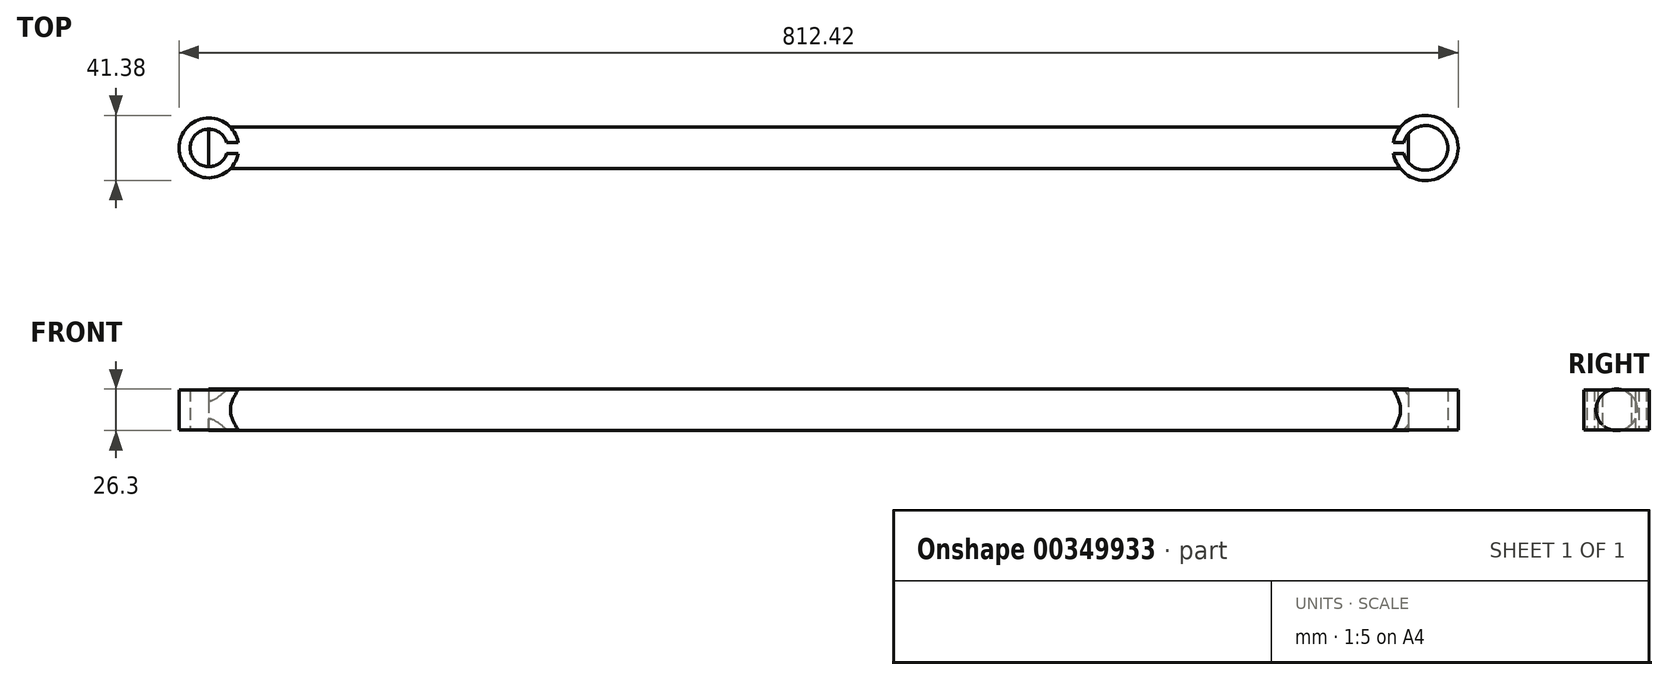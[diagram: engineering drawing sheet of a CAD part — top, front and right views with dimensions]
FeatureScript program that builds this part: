
annotation { "Feature Type Name" : "Feature", "Feature Type Description" : "" }
export const myFeature = defineFeature(function(context is Context, id is Id, definition is map)
    precondition{}
    {
        {
            var Q0;
            Q0=qCreatedBy(makeId("Right.planeOp"),FACE);
            var sketch = newSketch(context, id + "F0", { "sketchPlane" : qUnion([Q0])});
            skCircle(sketch, "E0", {"center": v(0, 0) * mm, "radius": 13.15 * mm});
            skSolve(sketch);
        }
        {
            var Q0;
            Q0 = qSketchRegion(id + "F0", true);
            extrude(context, id + "F1", {"entities" : qUnion([Q0]), "depth" : 762 * mm, "offsetDistance" : 25.4 * mm});
        }
        {
            var Q0;
            Q0=qCreatedBy(makeId("Top.planeOp"),FACE);
            var sketch = newSketch(context, id + "F2", { "sketchPlane" : qUnion([Q0])});
            skCircle(sketch, "E1", {"center": v(0, 0) * mm, "radius": 18.97 * mm});
            skCircle(sketch, "E2", {"center": v(772.77, 0) * mm, "radius": 20.69 * mm});
            skCircle(sketch, "E3", {"center": v(0, 0) * mm, "radius": 11.9 * mm});
            skCircle(sketch, "E4", {"center": v(772.77, 0) * mm, "radius": 14.19 * mm});
            skSolve(sketch);
        }
        {
            var Q0;
            Q0 = qSketchRegion(id + "F2", true);
            extrude(context, id + "F3", {"entities" : qUnion([Q0]), "operationType" : NewBodyOperationType.ADD, "endBound" : BoundingType.SYMMETRIC, "depth" : 25.4 * mm, "offsetDistance" : 25.4 * mm});
        }
    });
